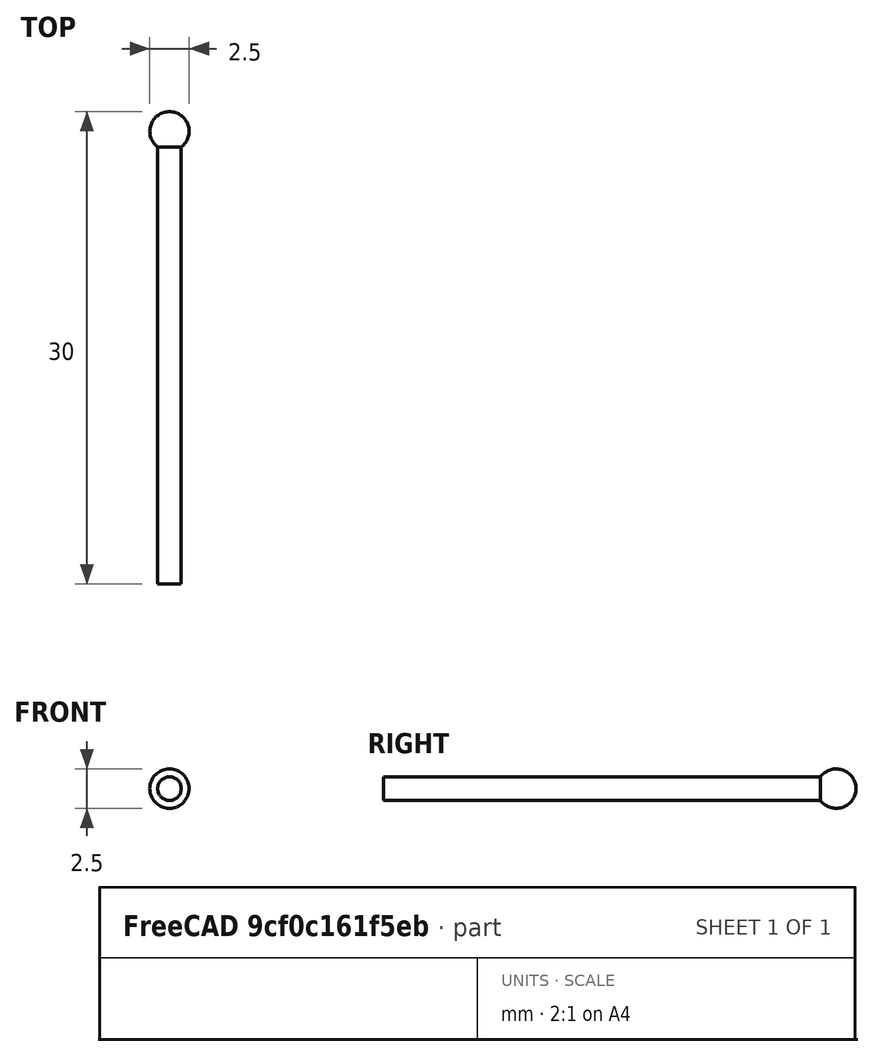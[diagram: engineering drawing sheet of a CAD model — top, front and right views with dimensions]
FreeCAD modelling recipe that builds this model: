
FCSTD DOCUMENT  (FreeCAD 0.19R24366 (Git))
Label: actuator_pushrod
License: All rights reserved
LicenseURL: http://en.wikipedia.org/wiki/All_rights_reserved
objects: Spreadsheet::Sheet×1, Sketcher::SketchObject×1, PartDesign::Revolution×1, PartDesign::Body×1, Mesh::Feature×1
note: 4 computed .brp shape members not serialized (recipe doc carries the construction recipe); baked Part::Feature solids carry a one-line shape summary decoded from their .brp

FEATURE [Spreadsheet::Sheet] Spreadsheet
  cells = A1=RodLength; B1(RodLength)==30mm; A2=RodDiameter; B2(RodDiameter)==1.5mm; A3=BallDiameter; B3(BallDiameter)==2.5mm
FEATURE [Sketcher::SketchObject] Sketch
  FullyConstrained = true
  MapMode = 5
  Support = -> [XY_Plane]
  expr: Constraints[11] = Spreadsheet.RodLength
  expr: Constraints[10] = 0.5 * Spreadsheet.BallDiameter
  expr: Constraints[9] = 0.5 * Spreadsheet.RodDiameter
  sketch-geometry (4):
    g0: LineSegment StartX=4e-16 StartY=0 StartZ=0 EndX=4e-16 EndY=30 EndZ=0
    g1: ArcOfCircle CenterX=0 CenterY=28.75 CenterZ=0 NormalX=0 NormalY=0 NormalZ=1 AngleXU=0 Radius=1.25 StartAngle=5.35589 EndAngle=7.85398
    g2: LineSegment StartX=0.75 StartY=27.75 StartZ=0 EndX=0.75 EndY=0 EndZ=0
    g3: LineSegment StartX=4e-16 StartY=0 StartZ=0 EndX=0.75 EndY=0 EndZ=0
  constraints (12):
    c: Vertical(g0)
    c: Coincident(g-1,g0)
    c: Coincident(g1,g0)
    c: PointOnObject(g1,g0)
    c: Vertical(g2)
    c: Horizontal(g3)
    c: Coincident(g0,g3)
    c: Coincident(g2,g3)
    c: Coincident(g1,g2)
    c: DistanceX(g3,g3) = 0.75
    c: Radius(g1) = 1.25
    c: DistanceY(g0,g0) = 30
FEATURE [PartDesign::Revolution] Revolution
  Angle = 360
  Axis = (0,1,0)
  Base = (0,0,0)
  Profile = -> Sketch
  ReferenceAxis = -> Sketch [V_Axis]
  Reversed = true
FEATURE [PartDesign::Body] Body
  Group = -> [Sketch,Revolution]
  Origin = -> Origin
  Tip = -> Revolution
FEATURE [Mesh::Feature] Mesh  label="Body (Meshed)"
